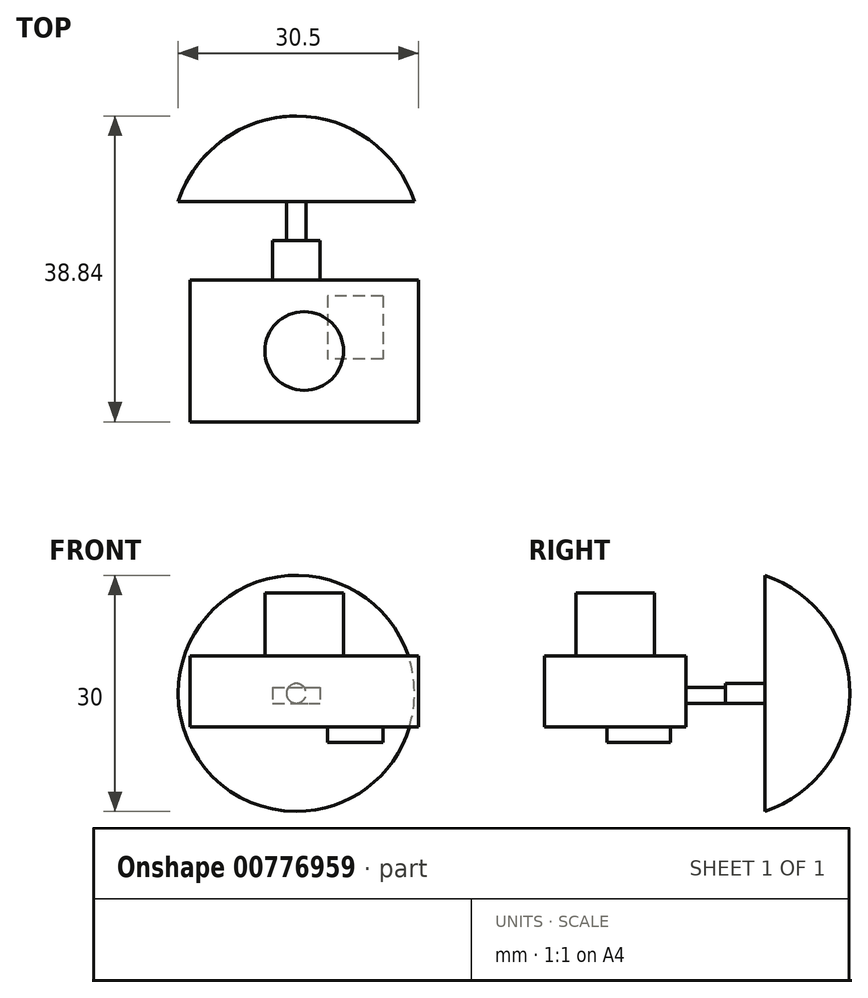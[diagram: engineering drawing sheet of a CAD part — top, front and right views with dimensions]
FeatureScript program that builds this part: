
annotation { "Feature Type Name" : "Feature", "Feature Type Description" : "" }
export const myFeature = defineFeature(function(context is Context, id is Id, definition is map)
    precondition{}
    {
        {
            var Q0;
            Q0=qCreatedBy(makeId("Top.planeOp"),FACE);
            var sketch = newSketch(context, id + "F0", { "sketchPlane" : qUnion([Q0])});
            skLineSegment(sketch, "E0.bottom", {"start": v(0, 0) * mm, "end": v(29, 0) * mm});
            skLineSegment(sketch, "E0.top", {"start": v(0, 18) * mm, "end": v(29, 18) * mm});
            skLineSegment(sketch, "E0.left", {"start": v(0, 0) * mm, "end": v(0, 18) * mm});
            skLineSegment(sketch, "E0.right", {"start": v(29, 0) * mm, "end": v(29, 18) * mm});
            skSolve(sketch);
        }
        {
            var Q0;
            Q0=qSketchRegion(id+"F0",true);
            extrude(context, id + "F1", {"entities" : qUnion([Q0]), "depth" : 9 * mm, "offsetDistance" : 25 * mm});
        }
        {
            var Q0;
            Q0=makeQuery(id+"F1.opExtrude","CAP_FACE",FACE,{"disambiguationData":[OSD([sQuery(id+"F0.wireOp",EDGE,"E0.bottom"),sQuery(id+"F0.wireOp",EDGE,"E0.top"),sQuery(id+"F0.wireOp",EDGE,"E0.left"),sQuery(id+"F0.wireOp",EDGE,"E0.right")])],"isStart":false});
            var sketch = newSketch(context, id + "F2", { "sketchPlane" : qUnion([Q0])});
            skCircle(sketch, "E1", {"center": v(14.5, 9) * mm, "radius": 5 * mm});
            skPoint(sketch, "E1.centerSnap0", {"position": v(14.5, 0) * mm});
            skPoint(sketch, "E1.centerSnap1", {"position": v(0, 9) * mm});
            skSolve(sketch);
        }
        {
            var Q0;
            Q0=qSketchRegion(id+"F2",true);
            extrude(context, id + "F3", {"entities" : qUnion([Q0]), "operationType" : NewBodyOperationType.ADD, "depth" : 8 * mm, "offsetDistance" : 25 * mm});
        }
        {
            var Q0;
            Q0=makeQuery(id+"F1.opExtrude","CAP_FACE",FACE,{"disambiguationData":[OSD([sQuery(id+"F0.wireOp",EDGE,"E0.bottom"),sQuery(id+"F0.wireOp",EDGE,"E0.top"),sQuery(id+"F0.wireOp",EDGE,"E0.left"),sQuery(id+"F0.wireOp",EDGE,"E0.right")])],"isStart":true});
            var sketch = newSketch(context, id + "F4", { "sketchPlane" : qUnion([Q0])});
            skLineSegment(sketch, "E2.bottom", {"start": v(24.5, -16) * mm, "end": v(17.5, -16) * mm});
            skLineSegment(sketch, "E2.top", {"start": v(24.5, -8) * mm, "end": v(17.5, -8) * mm});
            skLineSegment(sketch, "E2.left", {"start": v(24.5, -16) * mm, "end": v(24.5, -8) * mm});
            skLineSegment(sketch, "E2.right", {"start": v(17.5, -16) * mm, "end": v(17.5, -8) * mm});
            skSolve(sketch);
        }
        {
            var Q0;
            Q0=qSketchRegion(id+"F4",true);
            extrude(context, id + "F5", {"entities" : qUnion([Q0]), "operationType" : NewBodyOperationType.ADD, "depth" : 2 * mm, "offsetDistance" : 25 * mm});
        }
        {
            var Q0;
            Q0=makeQuery(id+"F1.opExtrude","SWEPT_FACE",FACE,{"disambiguationData":[OSD([sQuery(id+"F0.wireOp",EDGE,"E0.top")])]});
            var sketch = newSketch(context, id + "F6", { "sketchPlane" : qUnion([Q0])});
            skLineSegment(sketch, "E3.bottom", {"start": v(-10.5, 5) * mm, "end": v(-16.5, 5) * mm});
            skLineSegment(sketch, "E3.top", {"start": v(-10.5, 3) * mm, "end": v(-16.5, 3) * mm});
            skLineSegment(sketch, "E3.left", {"start": v(-10.5, 5) * mm, "end": v(-10.5, 3) * mm});
            skLineSegment(sketch, "E3.right", {"start": v(-16.5, 5) * mm, "end": v(-16.5, 3) * mm});
            skSolve(sketch);
        }
        {
            var Q0;
            Q0=qSketchRegion(id+"F6",true);
            extrude(context, id + "F7", {"entities" : qUnion([Q0]), "operationType" : NewBodyOperationType.ADD, "depth" : 5 * mm, "offsetDistance" : 25 * mm});
        }
        {
            var Q0;
            Q0=makeQuery(id+"F7.opExtrude","CAP_FACE",FACE,{"disambiguationData":[OSD([sQuery(id+"F6.wireOp",EDGE,"E3.bottom"),sQuery(id+"F6.wireOp",EDGE,"E3.top"),sQuery(id+"F6.wireOp",EDGE,"E3.left"),sQuery(id+"F6.wireOp",EDGE,"E3.right")])],"isStart":false});
            var sketch = newSketch(context, id + "F8", { "sketchPlane" : qUnion([Q0])});
            skCircle(sketch, "E4", {"center": v(-13.5, 4.25) * mm, "radius": 1.25 * mm});
            skPoint(sketch, "E4.centerSnap0", {"position": v(-13.5, 5) * mm});
            skSolve(sketch);
        }
        {
            var Q0;
            Q0=qSketchRegion(id+"F8",true);
            extrude(context, id + "F9", {"entities" : qUnion([Q0]), "operationType" : NewBodyOperationType.ADD, "depth" : 5 * mm, "offsetDistance" : 25 * mm});
        }
        {
            var Q0;
            Q0=makeQuery(id+"F9.opExtrude","CAP_FACE",FACE,{"disambiguationData":[OSD([sQuery(id+"F8.wireOp",EDGE,"E4")])],"isStart":false});
            var sketch = newSketch(context, id + "F10", { "sketchPlane" : qUnion([Q0])});
            skPoint(sketch, "E5", {"position": v(-13.5, 4.25) * mm});
            skSolve(sketch);
        }
        {
            var Q0;
            Q0=makeQuery(id+"F7.opExtrude","SWEPT_FACE",FACE,{"disambiguationData":[OSD([sQuery(id+"F6.wireOp",EDGE,"E3.top")])]});
            var Q1;
            Q1=sQuery(id+"F10.wireOp",VERTEX,"E5");
            cPlane(context, id + "F11", {"entities" : qUnion([Q0, Q1]), "cplaneType" : CPlaneType.PLANE_POINT, "offset" : 25 * mm, "width" : 150 * mm, "height" : 150 * mm});
        }
        {
            var Q0;
            Q0=qCreatedBy(id+"F11.planeOp",FACE);
            var sketch = newSketch(context, id + "F12", { "sketchPlane" : qUnion([Q0])});
            skLineSegment(sketch, "E6.0", {"start": v(14.75, -28) * mm, "end": v(12.25, -28) * mm});
            skPoint(sketch, "E6.1", {"position": v(13.5, -28) * mm});
            skLineSegment(sketch, "E7", {"start": v(28.5, -28) * mm, "end": v(-1.5, -28) * mm});
            skArc(sketch, "E8", {"start": v(-1.5, -28) * mm, "mid": v(13.5, -38.84) * mm, "end": v(28.5, -28) * mm});
            skLineSegment(sketch, "E9", {"start": v(13.5, -28) * mm, "end": v(13.5, -42.63) * mm, "construction": true});
            skLineSegment(sketch, "E10", {"start": v(13.5, -28) * mm, "end": v(13.5, -38.84) * mm});
            skSolve(sketch);
        }
        {
            var Q0;
            {var subQ3=sQuery(id+"F12.wireOp",EDGE,"E10");Q0=makeQuery(id+"F12.imprint","IMPRINT",FACE,{"disambiguationData":[TD([[makeQuery(id+"F12.imprint","IMPRINT",EDGE,{"derivedFrom":subQ3}),1.0]])]});}
            var Q1;
            Q1=sQuery(id+"F12.wireOp",EDGE,"E9");
            revolve(context, id + "F13", {"operationType" : NewBodyOperationType.ADD, "surfaceOperationType" : NewSurfaceOperationType.NEW, "entities" : qUnion([Q0]), "axis" : qUnion([Q1]), "revolveType" : RevolveType.FULL});
        }
    });
